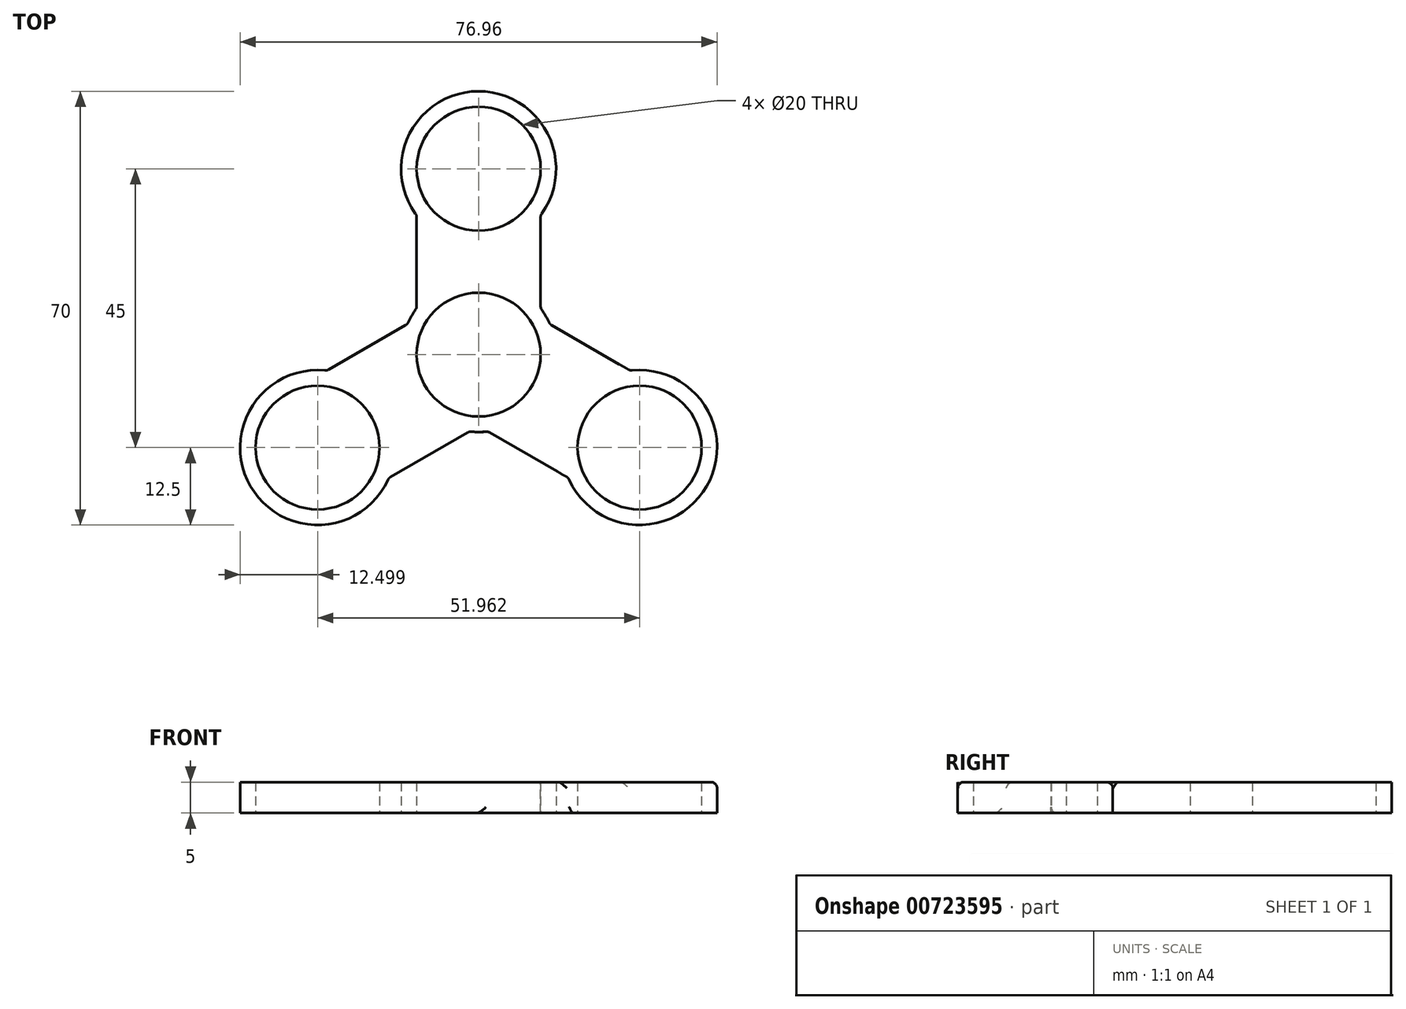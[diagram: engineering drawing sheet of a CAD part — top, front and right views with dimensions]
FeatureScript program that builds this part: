
annotation { "Feature Type Name" : "Feature", "Feature Type Description" : "" }
export const myFeature = defineFeature(function(context is Context, id is Id, definition is map)
    precondition{}
    {
        {
            var Q0;
            Q0=qCreatedBy(makeId("Top.planeOp"),FACE);
            var sketch = newSketch(context, id + "F0", { "sketchPlane" : qUnion([Q0])});
            skCircle(sketch, "E0", {"center": v(0, 0) * mm, "radius": 10 * mm});
            skCircle(sketch, "E1", {"center": v(0, 0) * mm, "radius": 12.5 * mm});
            skLineSegment(sketch, "E2.bottom", {"start": v(-10, 0) * mm, "end": v(10, 0) * mm});
            skLineSegment(sketch, "E2.top", {"start": v(-10, 30) * mm, "end": v(10, 30) * mm});
            skLineSegment(sketch, "E2.left", {"start": v(-10, 0) * mm, "end": v(-10, 30) * mm});
            skLineSegment(sketch, "E2.right", {"start": v(10, 0) * mm, "end": v(10, 30) * mm});
            skCircle(sketch, "E3", {"center": v(0, 30) * mm, "radius": 10 * mm});
            skCircle(sketch, "E4", {"center": v(0, 30) * mm, "radius": 12.5 * mm});
            skSolve(sketch);
        }
        {
            var Q0;
            Q0=qSketchRegion(id+"F0",true);
            extrude(context, id + "F1", {"entities" : qUnion([Q0]), "depth" : 5 * mm, "offsetDistance" : 25 * mm});
        }
        {
            var Q0;
            Q0=makeQuery(id+"F1.opExtrude","SWEPT_BODY",BODY,{"disambiguationData":[OSD([sQuery(id+"F0.wireOp",EDGE,"E0"),sQuery(id+"F0.wireOp",EDGE,"E1"),sQuery(id+"F0.wireOp",EDGE,"E2.left"),sQuery(id+"F0.wireOp",EDGE,"E2.right"),sQuery(id+"F0.wireOp",EDGE,"E3"),sQuery(id+"F0.wireOp",EDGE,"E4")])]});
            var Q1;
            Q1=makeQuery(id+"F1.opExtrude","CAP_EDGE",EDGE,{"disambiguationData":[OSD([sQuery(id+"F0.wireOp",EDGE,"E0")])],"isStart":true});
            circularPattern(context, id + "F2", {"entities" : qUnion([Q0]), "axis" : qUnion([Q1]), "angle" : 360 * degree, "instanceCount" : 3, "equalSpace" : true});
        }
        {
            var Q0;
            Q0=makeQuery(id+"F2.opPattern","COPY",BODY,{"derivedFrom":makeQuery(id+"F1.opExtrude","SWEPT_BODY",BODY,{"disambiguationData":[OSD([sQuery(id+"F0.wireOp",EDGE,"E0"),sQuery(id+"F0.wireOp",EDGE,"E1"),sQuery(id+"F0.wireOp",EDGE,"E2.left"),sQuery(id+"F0.wireOp",EDGE,"E2.right"),sQuery(id+"F0.wireOp",EDGE,"E3"),sQuery(id+"F0.wireOp",EDGE,"E4")])]}),"instanceName":"1"});
            var Q1;
            Q1=makeQuery(id+"F1.opExtrude","SWEPT_BODY",BODY,{"disambiguationData":[OSD([sQuery(id+"F0.wireOp",EDGE,"E0"),sQuery(id+"F0.wireOp",EDGE,"E1"),sQuery(id+"F0.wireOp",EDGE,"E2.left"),sQuery(id+"F0.wireOp",EDGE,"E2.right"),sQuery(id+"F0.wireOp",EDGE,"E3"),sQuery(id+"F0.wireOp",EDGE,"E4")])]});
            var Q2;
            Q2=makeQuery(id+"F2.opPattern","COPY",BODY,{"derivedFrom":makeQuery(id+"F1.opExtrude","SWEPT_BODY",BODY,{"disambiguationData":[OSD([sQuery(id+"F0.wireOp",EDGE,"E0"),sQuery(id+"F0.wireOp",EDGE,"E1"),sQuery(id+"F0.wireOp",EDGE,"E2.left"),sQuery(id+"F0.wireOp",EDGE,"E2.right"),sQuery(id+"F0.wireOp",EDGE,"E3"),sQuery(id+"F0.wireOp",EDGE,"E4")])]}),"instanceName":"2"});
            booleanBodies(context, id + "F3", {"operationType" : BooleanOperationType.UNION, "tools" : qUnion([Q0, Q1, Q2])});
        }
        {
            var Q0;
            Q0=makeQuery(id+"F2.opPattern","COPY",EDGE,{"derivedFrom":makeQuery(id+"F1.opExtrude","SWEPT_EDGE",EDGE,{"disambiguationData":[OSD([sQuery(id+"F0.wireOp",EDGE,"E2.left"),sQuery(id+"F0.wireOp",EDGE,"E4")])]}),"instanceName":"1"});
            var Q1;
            Q1=makeQuery(id+"F2.opPattern","COPY",EDGE,{"derivedFrom":makeQuery(id+"F1.opExtrude","SWEPT_EDGE",EDGE,{"disambiguationData":[OSD([sQuery(id+"F0.wireOp",EDGE,"E1"),sQuery(id+"F0.wireOp",EDGE,"E2.left")])]}),"instanceName":"1"});
            var Q2;
            {var subQ0=makeQuery(id+"F1.opExtrude","SWEPT_FACE",FACE,{"disambiguationData":[OSD([sQuery(id+"F0.wireOp",EDGE,"E1")])]});var subQ1=makeQuery(id+"F2.opPattern","COPY",FACE,{"derivedFrom":subQ0,"instanceName":"1"});Q2=makeQuery(id+"F3.opBoolean","INTERSECT",EDGE,{"disambiguationData":[topologyDisambiguationEdgeConnected([makeQuery(id+"F2.opPattern","COPY",FACE,{"derivedFrom":makeQuery(id+"F1.opExtrude","SWEPT_FACE",FACE,{"disambiguationData":[OSD([sQuery(id+"F0.wireOp",EDGE,"E2.right")])]}),"instanceName":"2"})])],"derivedFrom":[subQ0,subQ1]});}
            var Q3;
            Q3=makeQuery(id+"F2.opPattern","COPY",EDGE,{"derivedFrom":makeQuery(id+"F1.opExtrude","SWEPT_EDGE",EDGE,{"disambiguationData":[OSD([sQuery(id+"F0.wireOp",EDGE,"E2.right"),sQuery(id+"F0.wireOp",EDGE,"E4")])]}),"instanceName":"2"});
            var Q4;
            Q4=makeQuery(id+"F2.opPattern","COPY",EDGE,{"derivedFrom":makeQuery(id+"F1.opExtrude","SWEPT_EDGE",EDGE,{"disambiguationData":[OSD([sQuery(id+"F0.wireOp",EDGE,"E2.left"),sQuery(id+"F0.wireOp",EDGE,"E4")])]}),"instanceName":"2"});
            var Q5;
            {var subQ0=makeQuery(id+"F1.opExtrude","SWEPT_FACE",FACE,{"disambiguationData":[OSD([sQuery(id+"F0.wireOp",EDGE,"E1")])]});var subQ1=makeQuery(id+"F2.opPattern","COPY",FACE,{"derivedFrom":subQ0,"instanceName":"1"});Q5=makeQuery(id+"F3.opBoolean","INTERSECT",EDGE,{"disambiguationData":[topologyDisambiguationEdgeConnected([makeQuery(id+"F2.opPattern","COPY",FACE,{"derivedFrom":makeQuery(id+"F1.opExtrude","SWEPT_FACE",FACE,{"disambiguationData":[OSD([sQuery(id+"F0.wireOp",EDGE,"E2.left")])]}),"instanceName":"2"})])],"derivedFrom":[subQ0,subQ1]});}
            var Q6;
            {var subQ0=makeQuery(id+"F1.opExtrude","SWEPT_FACE",FACE,{"disambiguationData":[OSD([sQuery(id+"F0.wireOp",EDGE,"E1")])]});var subQ1=makeQuery(id+"F2.opPattern","COPY",FACE,{"derivedFrom":subQ0,"instanceName":"1"});Q6=makeQuery(id+"F3.opBoolean","INTERSECT",EDGE,{"disambiguationData":[topologyDisambiguationEdgeConnected([makeQuery(id+"F1.opExtrude","SWEPT_FACE",FACE,{"disambiguationData":[OSD([sQuery(id+"F0.wireOp",EDGE,"E2.right")])]})])],"derivedFrom":[subQ1,makeQuery(id+"F2.opPattern","COPY",FACE,{"derivedFrom":subQ0,"instanceName":"2"})]});}
            var Q7;
            Q7=makeQuery(id+"F1.opExtrude","SWEPT_EDGE",EDGE,{"disambiguationData":[OSD([sQuery(id+"F0.wireOp",EDGE,"E2.right"),sQuery(id+"F0.wireOp",EDGE,"E4")])]});
            var Q8;
            Q8=makeQuery(id+"F1.opExtrude","SWEPT_EDGE",EDGE,{"disambiguationData":[OSD([sQuery(id+"F0.wireOp",EDGE,"E2.left"),sQuery(id+"F0.wireOp",EDGE,"E4")])]});
            var Q9;
            {var subQ0=makeQuery(id+"F1.opExtrude","SWEPT_FACE",FACE,{"disambiguationData":[OSD([sQuery(id+"F0.wireOp",EDGE,"E1")])]});var subQ1=makeQuery(id+"F2.opPattern","COPY",FACE,{"derivedFrom":subQ0,"instanceName":"1"});Q9=makeQuery(id+"F3.opBoolean","INTERSECT",EDGE,{"disambiguationData":[topologyDisambiguationEdgeConnected([makeQuery(id+"F1.opExtrude","SWEPT_FACE",FACE,{"disambiguationData":[OSD([sQuery(id+"F0.wireOp",EDGE,"E2.left")])]})])],"derivedFrom":[subQ1,makeQuery(id+"F2.opPattern","COPY",FACE,{"derivedFrom":subQ0,"instanceName":"2"})]});}
            var Q10;
            Q10=makeQuery(id+"F2.opPattern","COPY",EDGE,{"derivedFrom":makeQuery(id+"F1.opExtrude","SWEPT_EDGE",EDGE,{"disambiguationData":[OSD([sQuery(id+"F0.wireOp",EDGE,"E1"),sQuery(id+"F0.wireOp",EDGE,"E2.right")])]}),"instanceName":"1"});
            var Q11;
            Q11=makeQuery(id+"F2.opPattern","COPY",EDGE,{"derivedFrom":makeQuery(id+"F1.opExtrude","SWEPT_EDGE",EDGE,{"disambiguationData":[OSD([sQuery(id+"F0.wireOp",EDGE,"E2.right"),sQuery(id+"F0.wireOp",EDGE,"E4")])]}),"instanceName":"1"});
            var Q12;
            Q12=makeQuery(id+"F2.opPattern","COPY",EDGE,{"derivedFrom":makeQuery(id+"F1.opExtrude","CAP_EDGE",EDGE,{"disambiguationData":[OSD([sQuery(id+"F0.wireOp",EDGE,"E4")])],"isStart":false}),"instanceName":"2"});
            var Q13;
            Q13=makeQuery(id+"F2.opPattern","COPY",EDGE,{"derivedFrom":makeQuery(id+"F1.opExtrude","CAP_EDGE",EDGE,{"disambiguationData":[OSD([sQuery(id+"F0.wireOp",EDGE,"E2.right")])],"isStart":true}),"instanceName":"2"});
            fillet(context, id + "F4", {"entities" : qUnion([Q0, Q1, Q2, Q3, Q4, Q5, Q6, Q7, Q8, Q9, Q10, Q11, Q12, Q13]), "radius" : 1 * mm, "tangentPropagation" : true, "allowEdgeOverflow" : false});
        }
    });
